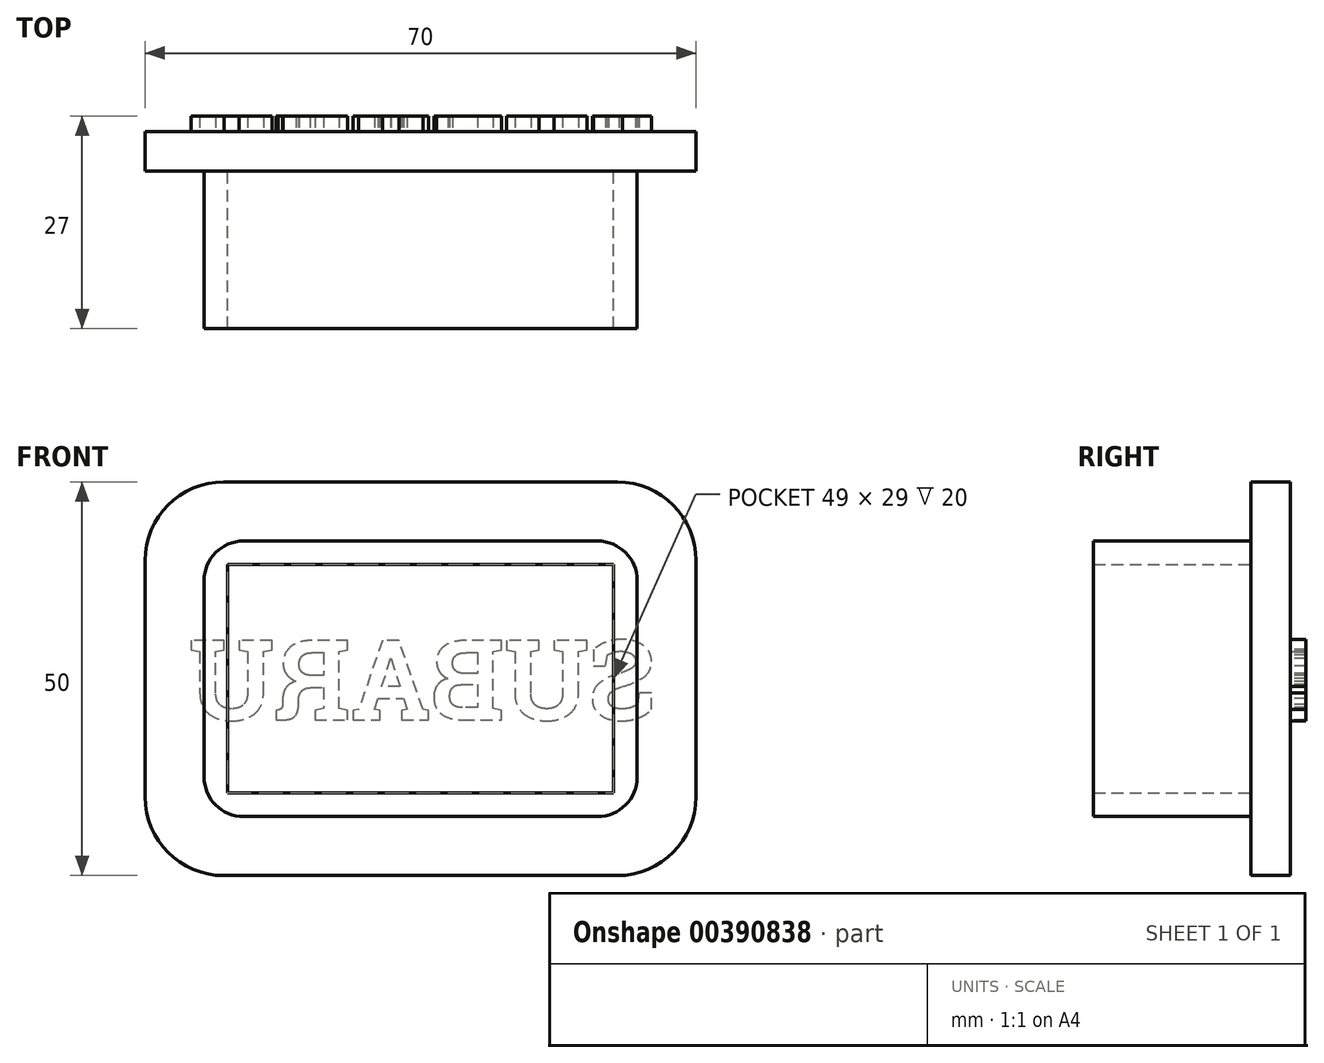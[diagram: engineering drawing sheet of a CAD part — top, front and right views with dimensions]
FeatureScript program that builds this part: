
annotation { "Feature Type Name" : "Feature", "Feature Type Description" : "" }
export const myFeature = defineFeature(function(context is Context, id is Id, definition is map)
    precondition{}
    {
        {
            var Q0;
            Q0=qCreatedBy(makeId("Front.planeOp"),FACE);
            var sketch = newSketch(context, id + "F0", { "sketchPlane" : qUnion([Q0])});
            skLineSegment(sketch, "E0.bottom", {"start": v(-35, -25) * mm, "end": v(35, -25) * mm});
            skLineSegment(sketch, "E0.top", {"start": v(-35, 25) * mm, "end": v(35, 25) * mm});
            skLineSegment(sketch, "E0.left", {"start": v(-35, -25) * mm, "end": v(-35, 25) * mm});
            skLineSegment(sketch, "E0.right", {"start": v(35, -25) * mm, "end": v(35, 25) * mm});
            skSolve(sketch);
        }
        {
            var Q0;
            Q0=makeQuery(id+"F0.imprint","IMPRINT",FACE,{"disambiguationData":[TD([[makeQuery(id+"F0.imprint","IMPRINT",EDGE,{"derivedFrom":sQuery(id+"F0.wireOp",EDGE,"E0.bottom")}),1.0]])]});
            extrude(context, id + "F1", {"entities" : qUnion([Q0]), "depth" : 5 * mm});
        }
        {
            var Q0;
            Q0=makeQuery(id+"F1.opExtrude","CAP_FACE",FACE,{"disambiguationData":[OSD([sQuery(id+"F0.wireOp",EDGE,"E0.bottom"),sQuery(id+"F0.wireOp",EDGE,"E0.top"),sQuery(id+"F0.wireOp",EDGE,"E0.left"),sQuery(id+"F0.wireOp",EDGE,"E0.right")])],"isStart":false});
            var sketch = newSketch(context, id + "F2", { "sketchPlane" : qUnion([Q0])});
            skLineSegment(sketch, "E1.bottom", {"start": v(-27.5, -17.5) * mm, "end": v(27.5, -17.5) * mm});
            skLineSegment(sketch, "E1.top", {"start": v(-27.5, 17.5) * mm, "end": v(27.5, 17.5) * mm});
            skLineSegment(sketch, "E1.left", {"start": v(-27.5, -17.5) * mm, "end": v(-27.5, 17.5) * mm});
            skLineSegment(sketch, "E1.right", {"start": v(27.5, -17.5) * mm, "end": v(27.5, 17.5) * mm});
            skLineSegment(sketch, "E2.bottom", {"start": v(-24.5, -14.5) * mm, "end": v(24.5, -14.5) * mm});
            skLineSegment(sketch, "E2.top", {"start": v(-24.5, 14.5) * mm, "end": v(24.5, 14.5) * mm});
            skLineSegment(sketch, "E2.left", {"start": v(-24.5, -14.5) * mm, "end": v(-24.5, 14.5) * mm});
            skLineSegment(sketch, "E2.right", {"start": v(24.5, -14.5) * mm, "end": v(24.5, 14.5) * mm});
            skSolve(sketch);
        }
        {
            var Q0;
            Q0=makeQuery(id+"F2.imprint","IMPRINT",FACE,{"disambiguationData":[TD([[makeQuery(id+"F2.imprint","IMPRINT",EDGE,{"derivedFrom":sQuery(id+"F2.wireOp",EDGE,"E1.bottom")}),1.0]])]});
            extrude(context, id + "F3", {"entities" : qUnion([Q0]), "operationType" : NewBodyOperationType.ADD, "depth" : 20 * mm});
        }
        {
            var Q0;
            Q0=makeQuery(id+"F1.opExtrude","SWEPT_EDGE",EDGE,{"disambiguationData":[OSD([sQuery(id+"F0.wireOp",EDGE,"E0.top"),sQuery(id+"F0.wireOp",EDGE,"E0.right")])]});
            var Q1;
            Q1=makeQuery(id+"F1.opExtrude","SWEPT_EDGE",EDGE,{"disambiguationData":[OSD([sQuery(id+"F0.wireOp",EDGE,"E0.bottom"),sQuery(id+"F0.wireOp",EDGE,"E0.right")])]});
            var Q2;
            Q2=makeQuery(id+"F1.opExtrude","SWEPT_EDGE",EDGE,{"disambiguationData":[OSD([sQuery(id+"F0.wireOp",EDGE,"E0.bottom"),sQuery(id+"F0.wireOp",EDGE,"E0.left")])]});
            var Q3;
            Q3=makeQuery(id+"F1.opExtrude","SWEPT_EDGE",EDGE,{"disambiguationData":[OSD([sQuery(id+"F0.wireOp",EDGE,"E0.top"),sQuery(id+"F0.wireOp",EDGE,"E0.left")])]});
            fillet(context, id + "F4", {"entities" : qUnion([Q0, Q1, Q2, Q3]), "radius" : 10 * mm, "tangentPropagation" : true, "allowEdgeOverflow" : false});
        }
        {
            var Q0;
            Q0=makeQuery(id+"F3.opExtrude","SWEPT_EDGE",EDGE,{"disambiguationData":[OSD([sQuery(id+"F2.wireOp",EDGE,"E1.top"),sQuery(id+"F2.wireOp",EDGE,"E1.right")])]});
            var Q1;
            Q1=makeQuery(id+"F3.opExtrude","SWEPT_EDGE",EDGE,{"disambiguationData":[OSD([sQuery(id+"F2.wireOp",EDGE,"E1.top"),sQuery(id+"F2.wireOp",EDGE,"E1.left")])]});
            var Q2;
            Q2=makeQuery(id+"F3.opExtrude","SWEPT_EDGE",EDGE,{"disambiguationData":[OSD([sQuery(id+"F2.wireOp",EDGE,"E1.bottom"),sQuery(id+"F2.wireOp",EDGE,"E1.left")])]});
            var Q3;
            Q3=makeQuery(id+"F3.opExtrude","SWEPT_EDGE",EDGE,{"disambiguationData":[OSD([sQuery(id+"F2.wireOp",EDGE,"E1.bottom"),sQuery(id+"F2.wireOp",EDGE,"E1.right")])]});
            fillet(context, id + "F5", {"entities" : qUnion([Q0, Q1, Q2, Q3]), "radius" : 5 * mm, "tangentPropagation" : true, "allowEdgeOverflow" : false});
        }
        {
            var Q0;
            Q0=makeQuery(id+"F1.opExtrude","CAP_FACE",FACE,{"disambiguationData":[OSD([sQuery(id+"F0.wireOp",EDGE,"E0.bottom"),sQuery(id+"F0.wireOp",EDGE,"E0.top"),sQuery(id+"F0.wireOp",EDGE,"E0.left"),sQuery(id+"F0.wireOp",EDGE,"E0.right")])],"isStart":true});
            var sketch = newSketch(context, id + "F6", { "sketchPlane" : qUnion([Q0])});
            skText(sketch, "E3", { "text": "SUBARU", "fontName": "RobotoSlab-Bold.ttf"});
            const initialGuessF6  = {"E3": [-0.03, -0.00521, 1, 0, 0.01021]};
            skSetInitialGuess(sketch, initialGuessF6);
            skSolve(sketch);
        }
        {
            var Q0;
            Q0 = qSketchRegion(id + "F6", true);
            extrude(context, id + "F7", {"entities" : qUnion([Q0]), "operationType" : NewBodyOperationType.ADD, "depth" : 2 * mm});
        }
    });
